annotation { "Feature Type Name" : "Feature", "Feature Type Description" : "" }
export const myFeature = defineFeature(function(context is Context, id is Id, definition is map)
    precondition{}
    {
        {
            var Q0;
            Q0=qCreatedBy(makeId("Right.planeOp"),FACE);
            var sketch = newSketch(context, id + "F0", { "sketchPlane" : qUnion([Q0])});
            skLineSegment(sketch, "E0.bottom", {"start": v(-177.03, -97.3) * mm, "end": v(-174.73, -97.3) * mm});
            skLineSegment(sketch, "E0.top", {"start": v(-177.03, -147.3) * mm, "end": v(30.27, -147.3) * mm});
            skLineSegment(sketch, "E0.left", {"start": v(-177.03, -97.3) * mm, "end": v(-177.03, -147.3) * mm});
            skLineSegment(sketch, "E1", {"start": v(30.27, -147.3) * mm, "end": v(30.27, -97.3) * mm, "construction": true});
            skLineSegment(sketch, "E2", {"start": v(-14.73, -97.3) * mm, "end": v(-14.73, -147.3) * mm, "construction": true});
            skLineSegment(sketch, "E3", {"start": v(-104.73, -97.3) * mm, "end": v(-104.73, -147.3) * mm, "construction": true});
            skLineSegment(sketch, "E4", {"start": v(-159.73, -97.3) * mm, "end": v(-159.73, -147.3) * mm, "construction": true});
            skArc(sketch, "E5", {"start": v(-174.73, -97.3) * mm, "mid": v(-159.73, -82.3) * mm, "end": v(-144.73, -97.3) * mm});
            skArc(sketch, "E6", {"start": v(-119.73, -97.3) * mm, "mid": v(-104.73, -82.3) * mm, "end": v(-89.73, -97.3) * mm});
            skArc(sketch, "E7", {"start": v(-29.73, -97.3) * mm, "mid": v(-14.73, -82.3) * mm, "end": v(0.27, -97.3) * mm});
            skLineSegment(sketch, "E8.trimOffspring", {"start": v(-144.73, -97.3) * mm, "end": v(-119.73, -97.3) * mm});
            skLineSegment(sketch, "E9.trimOffspring", {"start": v(-89.73, -97.3) * mm, "end": v(-29.73, -97.3) * mm});
            skLineSegment(sketch, "E10.trimOffspring", {"start": v(0.27, -97.3) * mm, "end": v(30.27, -97.3) * mm});
            skLineSegment(sketch, "E11.MirrorCS", {"start": v(237.57, -97.3) * mm, "end": v(235.27, -97.3) * mm});
            skLineSegment(sketch, "E12.MirrorCS", {"start": v(237.57, -97.3) * mm, "end": v(237.57, -147.3) * mm});
            skArc(sketch, "E13.MirrorCS", {"start": v(180.27, -97.3) * mm, "mid": v(165.27, -82.3) * mm, "end": v(150.27, -97.3) * mm});
            skLineSegment(sketch, "E14.MirrorCS", {"start": v(60.27, -97.3) * mm, "end": v(30.27, -97.3) * mm});
            skLineSegment(sketch, "E15.MirrorCS", {"start": v(237.57, -147.3) * mm, "end": v(30.27, -147.3) * mm});
            skLineSegment(sketch, "E16.MirrorCS", {"start": v(150.27, -97.3) * mm, "end": v(90.27, -97.3) * mm});
            skLineSegment(sketch, "E17.MirrorCS", {"start": v(205.27, -97.3) * mm, "end": v(180.27, -97.3) * mm});
            skArc(sketch, "E18.MirrorCS", {"start": v(90.27, -97.3) * mm, "mid": v(75.27, -82.3) * mm, "end": v(60.27, -97.3) * mm});
            skLineSegment(sketch, "E19.MirrorCS", {"start": v(75.27, -97.3) * mm, "end": v(75.27, -147.3) * mm, "construction": true});
            skArc(sketch, "E20.MirrorCS", {"start": v(235.27, -97.3) * mm, "mid": v(220.27, -82.3) * mm, "end": v(205.27, -97.3) * mm});
            skLineSegment(sketch, "E21.MirrorCS", {"start": v(220.27, -97.3) * mm, "end": v(220.27, -147.3) * mm, "construction": true});
            skLineSegment(sketch, "E22.MirrorCS", {"start": v(165.27, -97.3) * mm, "end": v(165.27, -147.3) * mm, "construction": true});
            skCircle(sketch, "E23", {"center": v(-159.73, -97.3) * mm, "radius": 4 * mm});
            skCircle(sketch, "E24", {"center": v(-104.73, -97.3) * mm, "radius": 4 * mm});
            skCircle(sketch, "E25", {"center": v(-14.73, -97.3) * mm, "radius": 4 * mm});
            skCircle(sketch, "E26.MirrorC", {"center": v(75.27, -97.3) * mm, "radius": 4 * mm});
            skCircle(sketch, "E27.MirrorC", {"center": v(165.27, -97.3) * mm, "radius": 4 * mm});
            skCircle(sketch, "E28.MirrorC", {"center": v(220.27, -97.3) * mm, "radius": 4 * mm});
            skText(sketch, "E29", { "text": "BARCELONA", "fontName": "OpenSans-Regular.ttf"});
            skText(sketch, "E30", { "text": "REAL MADRID", "fontName": "OpenSans-Regular.ttf"});
            skLineSegment(sketch, "E31", {"start": v(-177.03, -122.3) * mm, "end": v(237.57, -122.3) * mm, "construction": true});
            skLineSegment(sketch, "E32", {"start": v(-144.73, -97.3) * mm, "end": v(-144.73, -147.3) * mm, "construction": true});
            skLineSegment(sketch, "E33.bottom", {"start": v(-128.38, -112.3) * mm, "end": v(-161.08, -112.3) * mm});
            skLineSegment(sketch, "E33.top", {"start": v(-128.38, -132.3) * mm, "end": v(-161.08, -132.3) * mm});
            skLineSegment(sketch, "E33.left", {"start": v(-128.38, -112.3) * mm, "end": v(-128.38, -132.3) * mm});
            skLineSegment(sketch, "E33.right", {"start": v(-161.08, -112.3) * mm, "end": v(-161.08, -132.3) * mm});
            skPoint(sketch, "E33.middle", {"position": v(-144.73, -122.3) * mm});
            skLineSegment(sketch, "E34.MirrorCS", {"start": v(188.92, -112.3) * mm, "end": v(221.62, -112.3) * mm});
            skLineSegment(sketch, "E35.MirrorCS", {"start": v(188.92, -132.3) * mm, "end": v(221.62, -132.3) * mm});
            skPoint(sketch, "E36.MirrorP", {"position": v(205.27, -122.3) * mm});
            skLineSegment(sketch, "E37.MirrorCS", {"start": v(221.62, -112.3) * mm, "end": v(221.62, -132.3) * mm});
            skLineSegment(sketch, "E38.MirrorCS", {"start": v(188.92, -112.3) * mm, "end": v(188.92, -132.3) * mm});
            const initialGuessF0  = {"E29": [-0.11082, -0.1323, 1, 0, 0.0151], "E30": [0.04064, -0.1323, 1, 0, 0.0151]};
            skSetInitialGuess(sketch, initialGuessF0);
            skSolve(sketch);
        }
        {
            var Q0;
            Q0 = qSketchRegion(id + "F0", true);
            extrude(context, id + "F1", {"entities" : qUnion([Q0]), "depth" : 12.7 * mm, "offsetDistance" : 25 * mm});
        }
    });